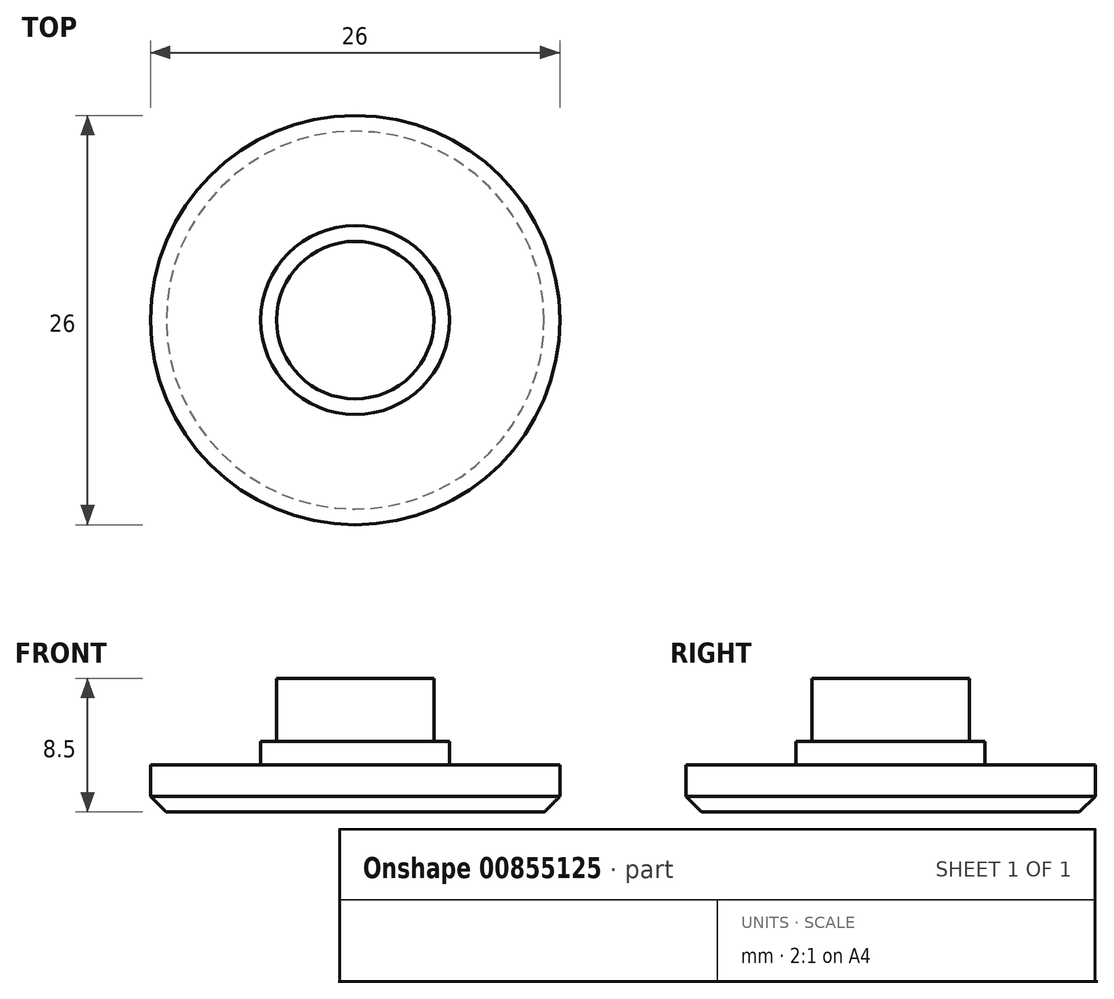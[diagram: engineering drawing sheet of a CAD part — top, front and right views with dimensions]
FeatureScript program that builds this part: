
annotation { "Feature Type Name" : "Feature", "Feature Type Description" : "" }
export const myFeature = defineFeature(function(context is Context, id is Id, definition is map)
    precondition{}
    {
        {
            var Q0;
            Q0=qCreatedBy(makeId("Top.planeOp"),FACE);
            var sketch = newSketch(context, id + "F0", { "sketchPlane" : qUnion([Q0])});
            skCircle(sketch, "E0", {"center": v(0, 0) * mm, "radius": 13 * mm});
            skSolve(sketch);
        }
        {
            var Q0;
            Q0=makeQuery(id+"F0.imprint","IMPRINT",FACE,{"disambiguationData":[TD([[makeQuery(id+"F0.imprint","IMPRINT",EDGE,{"derivedFrom":sQuery(id+"F0.wireOp",EDGE,"E0")}),1.0]])]});
            extrude(context, id + "F1", {"entities" : qUnion([Q0]), "depth" : 3 * mm, "offsetDistance" : 25.4 * mm});
        }
        {
            var Q0;
            Q0=makeQuery(id+"F1.opExtrude","CAP_FACE",FACE,{"disambiguationData":[OSD([sQuery(id+"F0.wireOp",EDGE,"E0")])],"isStart":false});
            var sketch = newSketch(context, id + "F2", { "sketchPlane" : qUnion([Q0])});
            skCircle(sketch, "E1", {"center": v(0, 0) * mm, "radius": 6 * mm});
            skSolve(sketch);
        }
        {
            var Q0;
            Q0=makeQuery(id+"F2.imprint","IMPRINT",FACE,{"disambiguationData":[TD([[makeQuery(id+"F2.imprint","IMPRINT",EDGE,{"derivedFrom":sQuery(id+"F2.wireOp",EDGE,"E1")}),1.0]])]});
            extrude(context, id + "F3", {"entities" : qUnion([Q0]), "operationType" : NewBodyOperationType.ADD, "depth" : 1.5 * mm, "offsetDistance" : 25 * mm});
        }
        {
            var Q0;
            Q0=makeQuery(id+"F3.opExtrude","CAP_FACE",FACE,{"disambiguationData":[OSD([sQuery(id+"F2.wireOp",EDGE,"E1")])],"isStart":false});
            var sketch = newSketch(context, id + "F4", { "sketchPlane" : qUnion([Q0])});
            skCircle(sketch, "E2", {"center": v(0, 0) * mm, "radius": 5 * mm});
            skSolve(sketch);
        }
        {
            var Q0;
            Q0=makeQuery(id+"F4.imprint","IMPRINT",FACE,{"disambiguationData":[TD([[makeQuery(id+"F4.imprint","IMPRINT",EDGE,{"derivedFrom":sQuery(id+"F4.wireOp",EDGE,"E2")}),1.0]])]});
            extrude(context, id + "F5", {"entities" : qUnion([Q0]), "operationType" : NewBodyOperationType.ADD, "depth" : 4 * mm, "offsetDistance" : 25 * mm});
        }
        {
            var Q0;
            Q0=makeQuery(id+"F1.opExtrude","CAP_EDGE",EDGE,{"disambiguationData":[OSD([sQuery(id+"F0.wireOp",EDGE,"E0")])],"isStart":true});
            chamfer(context, id + "F6", {"entities" : qUnion([Q0]), "width" : 1 * mm, "tangentPropagation" : true});
        }
    });
